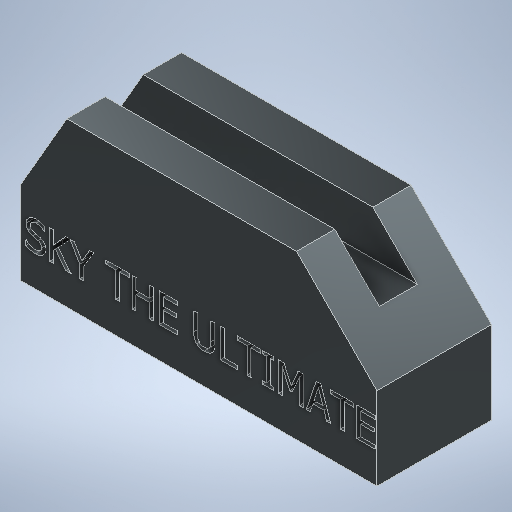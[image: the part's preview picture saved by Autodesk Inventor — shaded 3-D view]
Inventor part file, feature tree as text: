
AUTODESK INVENTOR PART (.ipt)
format: ipt  version: 2025.2 (Build 292293000, 293)  size: 468,480 bytes
history: native  units: in
note: dims shown in document units (in); Inventor stores cm internally (conversion verified against a paired STEP export)
features: sketch x7, projected_geometry x3, extrude x2, rib x1, emboss x1
ambient origin geometry x8: Origin, YZ Plane, XZ Plane, XY Plane, X Axis, Y Axis, Z Axis, Center Point
bodies: Solid1 (feature_tree)
feature tree (14):
  extrude  "Extrusion1"  Depth=2.2047in
  sketch  "Sketch2"  dims[d2=0.7087in d3=0.0in d6=150.0deg]
  rib  "Rib1"
  sketch  "Sketch4"  dims[d8=1.4201in]
  sketch  "Sketch5"  dims[d11=0.0394in d12=0.7087in d13=0.0in d14=0.0in d15=0.0394in d16=0.0394in]
  extrude  "Extrusion2"  TaperAngle=150.0deg  [1 undecoded]
  emboss  "Emboss1"
  sketch  "Sketch1"  dims[d0=2.2047in d1=0.5118in]
  sketch  "Sketch3"  dims[d7=135.0deg]
  projected_geometry  "Projected Loop1"
  projected_geometry  "Projected Loop2"
  projected_geometry  "Projected Loop3"
  sketch  "Sketch6"  dims[d17=1.4201in]
  sketch  "Sketch7"  dims[d18=0.7087in d19=1.8504in d20=0.2362in d21=0.2362in d22=0.2953in d23=0.2756in d24=0.0in d25=0.0787in d26=0.0in]
note: 1 required parameter value undecoded (feature->parameter linkage not recoverable at this tier; creation-order binding heuristic only, values carry confidence <= 0.55)
